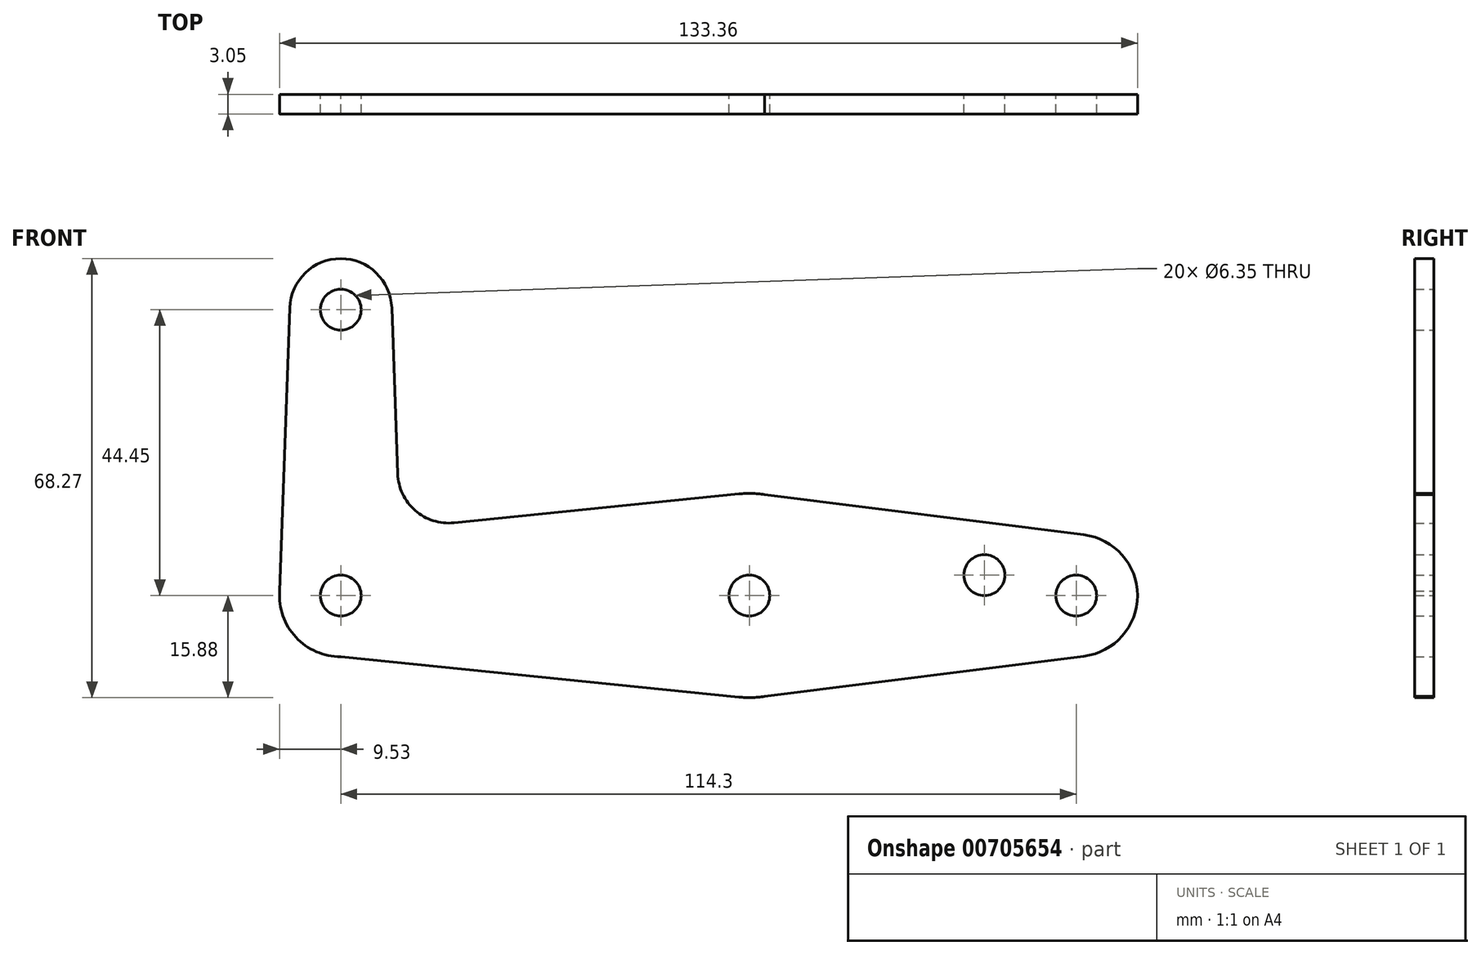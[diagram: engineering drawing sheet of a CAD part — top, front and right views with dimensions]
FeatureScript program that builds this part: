
annotation { "Feature Type Name" : "Feature", "Feature Type Description" : "" }
export const myFeature = defineFeature(function(context is Context, id is Id, definition is map)
    precondition{}
    {
        {
            var Q0;
            Q0=qCreatedBy(makeId("Front.planeOp"),FACE);
            var sketch = newSketch(context, id + "F0", { "sketchPlane" : qUnion([Q0])});
            skLineSegment(sketch, "E0", {"start": v(0, 0) * mm, "end": v(63.5, 0) * mm});
            skLineSegment(sketch, "E1", {"start": v(0, 0) * mm, "end": v(114.3, 0) * mm, "construction": true});
            skLineSegment(sketch, "E2", {"start": v(0, 0) * mm, "end": v(0, 44.45) * mm, "construction": true});
            skCircle(sketch, "E3", {"center": v(63.5, 0) * mm, "radius": 15.88 * mm});
            skCircle(sketch, "E4", {"center": v(114.3, 0) * mm, "radius": 9.53 * mm});
            skCircle(sketch, "E5", {"center": v(0, 0) * mm, "radius": 9.53 * mm});
            skCircle(sketch, "E6", {"center": v(0, 44.45) * mm, "radius": 7.94 * mm});
            skLineSegment(sketch, "E7", {"start": v(0, -9.53) * mm, "end": v(61.9, -15.8) * mm});
            skLineSegment(sketch, "E8", {"start": v(61.9, -15.8) * mm, "end": v(65.1, -15.8) * mm});
            skLineSegment(sketch, "E9", {"start": v(65.1, -15.8) * mm, "end": v(115.49, -9.45) * mm});
            skLineSegment(sketch, "E10", {"start": v(17.6, 11.3) * mm, "end": v(61.9, 15.8) * mm});
            skLineSegment(sketch, "E11", {"start": v(61.9, 15.8) * mm, "end": v(65.1, 15.8) * mm});
            skLineSegment(sketch, "E12", {"start": v(65.1, 15.8) * mm, "end": v(115.49, 9.45) * mm});
            skLineSegment(sketch, "E13", {"start": v(8.85, 18.93) * mm, "end": v(7.93, 44.73) * mm});
            skLineSegment(sketch, "E14", {"start": v(-9.53, 0) * mm, "end": v(-7.93, 44.73) * mm});
            skCircle(sketch, "E15", {"center": v(0, 44.45) * mm, "radius": 3.18 * mm});
            skCircle(sketch, "E16", {"center": v(0, 0) * mm, "radius": 3.18 * mm});
            skCircle(sketch, "E17", {"center": v(63.5, 0) * mm, "radius": 3.18 * mm});
            skCircle(sketch, "E18", {"center": v(114.3, 0) * mm, "radius": 3.18 * mm});
            skArc(sketch, "E19.filletArc", {"start": v(8.85, 18.93) * mm, "mid": v(11.57, 13.22) * mm, "end": v(17.6, 11.3) * mm});
            skLineSegment(sketch, "E20", {"start": v(63.5, 0) * mm, "end": v(100.03, 0) * mm});
            skLineSegment(sketch, "E21", {"start": v(100.03, 0) * mm, "end": v(100.03, 3.18) * mm});
            skCircle(sketch, "E22", {"center": v(100.03, 3.18) * mm, "radius": 3.18 * mm});
            skSolve(sketch);
        }
        {
            var Q0;
            Q0 = qSketchRegion(id + "F0", true);
            extrude(context, id + "F1", {"entities" : qUnion([Q0]), "depth" : 3.05 * mm, "offsetDistance" : 25.4 * mm});
        }
    });
